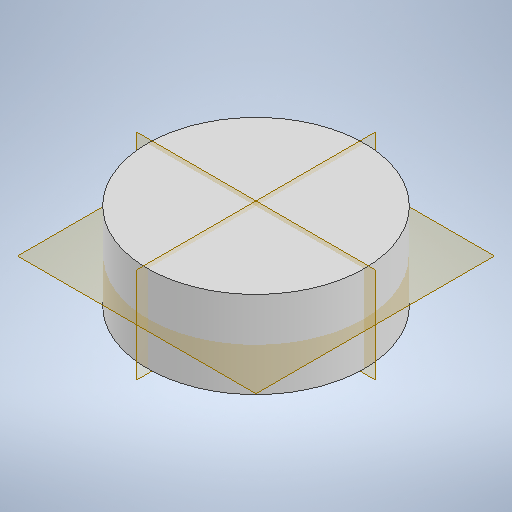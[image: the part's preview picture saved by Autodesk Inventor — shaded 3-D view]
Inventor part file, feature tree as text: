
AUTODESK INVENTOR PART (.ipt)
format: ipt  version: 2025.2 (Build 292293000, 293)  size: 219,648 bytes
history: native  units: mm
features: other x1, extrude x1, sketch x1
ambient origin geometry x8: Origin, YZ Plane, XZ Plane, XY Plane, X Axis, Y Axis, Z Axis, Center Point
bodies: Body1 (feature_tree)
feature tree (3):
  other  "Sólido1"
  extrude  "Extrusão1"  Depth=2.0mm TaperAngle=0.0deg
  sketch  "Esboço1"  dims[d0=5.0mm d1=2.0mm d2=0.0mm]
